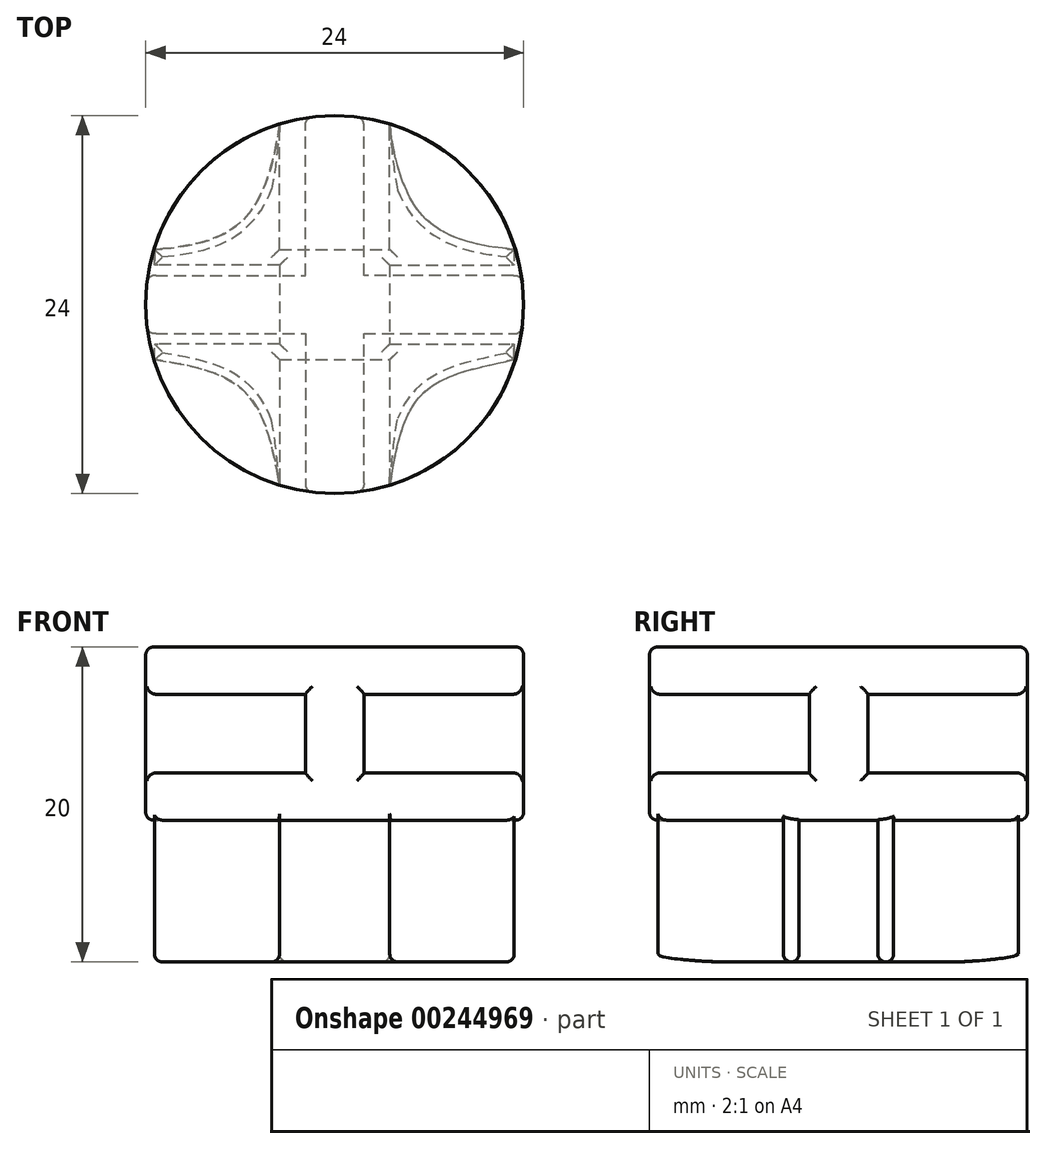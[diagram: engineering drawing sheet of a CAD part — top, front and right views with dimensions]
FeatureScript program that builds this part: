
annotation { "Feature Type Name" : "Feature", "Feature Type Description" : "" }
export const myFeature = defineFeature(function(context is Context, id is Id, definition is map)
    precondition{}
    {
        {
            var Q0;
            Q0=qCreatedBy(makeId("Top.planeOp"),FACE);
            var sketch = newSketch(context, id + "F0", { "sketchPlane" : qUnion([Q0])});
            skCircle(sketch, "E0", {"center": v(0, 0) * mm, "radius": 12 * mm});
            skSolve(sketch);
        }
        {
            var Q0;
            Q0=makeQuery(id+"F0.imprint","IMPRINT",FACE,{"disambiguationData":[TD([[makeQuery(id+"F0.imprint","IMPRINT",EDGE,{"derivedFrom":sQuery(id+"F0.wireOp",EDGE,"E0")}),1.0]])]});
            extrude(context, id + "F1", {"entities" : qUnion([Q0]), "depth" : 3 * mm});
        }
        {
            var Q0;
            Q0=qCreatedBy(makeId("Top.planeOp"),FACE);
            var sketch = newSketch(context, id + "F2", { "sketchPlane" : qUnion([Q0])});
            skCircle(sketch, "E1", {"center": v(0, 0) * mm, "radius": 12 * mm});
            skLineSegment(sketch, "E2", {"start": v(1.86, 11.86) * mm, "end": v(1.86, 1.86) * mm});
            skLineSegment(sketch, "E3", {"start": v(1.86, 1.86) * mm, "end": v(11.86, 1.86) * mm});
            skLineSegment(sketch, "E4", {"start": v(11.86, -1.86) * mm, "end": v(1.86, -1.86) * mm});
            skLineSegment(sketch, "E5", {"start": v(1.86, -1.86) * mm, "end": v(1.86, -11.86) * mm});
            skLineSegment(sketch, "E6", {"start": v(-1.86, 11.86) * mm, "end": v(-1.86, 1.86) * mm});
            skLineSegment(sketch, "E7", {"start": v(-1.86, 1.86) * mm, "end": v(-11.86, 1.86) * mm});
            skLineSegment(sketch, "E8", {"start": v(-1.86, -11.86) * mm, "end": v(-1.86, -1.86) * mm});
            skLineSegment(sketch, "E9", {"start": v(-1.86, -1.86) * mm, "end": v(-11.86, -1.86) * mm});
            skSolve(sketch);
        }
        {
            var Q0;
            {var subQ5=sQuery(id+"F2.wireOp",EDGE,"E2");Q0=makeQuery(id+"F2.imprint","IMPRINT",FACE,{"disambiguationData":[TD([[makeQuery(id+"F2.imprint","IMPRINT",EDGE,{"derivedFrom":subQ5}),-1.0]])]});}
            extrude(context, id + "F3", {"entities" : qUnion([Q0]), "operationType" : NewBodyOperationType.ADD, "depth" : 8 * mm});
        }
        {
            var Q0;
            Q0=makeQuery(id+"F3.opExtrude","CAP_FACE",FACE,{"disambiguationData":[OSD([sQuery(id+"F2.wireOp",EDGE,"E1"),sQuery(id+"F2.wireOp",EDGE,"E2"),sQuery(id+"F2.wireOp",EDGE,"E3"),sQuery(id+"F2.wireOp",EDGE,"E4"),sQuery(id+"F2.wireOp",EDGE,"E5"),sQuery(id+"F2.wireOp",EDGE,"E6"),sQuery(id+"F2.wireOp",EDGE,"E7"),sQuery(id+"F2.wireOp",EDGE,"E8"),sQuery(id+"F2.wireOp",EDGE,"E9")])],"isStart":false});
            var sketch = newSketch(context, id + "F4", { "sketchPlane" : qUnion([Q0])});
            skCircle(sketch, "E10", {"center": v(0, 0) * mm, "radius": 12 * mm});
            skSolve(sketch);
        }
        {
            var Q0;
            {var subQ1=makeQuery(id+"F3.opExtrude","CAP_EDGE",EDGE,{"disambiguationData":[OSD([sQuery(id+"F2.wireOp",EDGE,"E8")])],"isStart":false});Q0=makeQuery(id+"F4.imprint","IMPRINT",FACE,{"disambiguationData":[TD([[makeQuery(id+"F4.imprint","IMPRINT",EDGE,{"derivedFrom":subQ1}),1.0]])]});}
            var Q1;
            {var subQ6=makeQuery(id+"F3.opExtrude","CAP_EDGE",EDGE,{"disambiguationData":[OSD([sQuery(id+"F2.wireOp",EDGE,"E2")])],"isStart":false});Q1=makeQuery(id+"F4.imprint","IMPRINT",FACE,{"disambiguationData":[TD([[makeQuery(id+"F4.imprint","IMPRINT",EDGE,{"derivedFrom":subQ6}),-1.0]])]});}
            var Q2;
            {var subQ1=makeQuery(id+"F3.opExtrude","CAP_EDGE",EDGE,{"disambiguationData":[OSD([sQuery(id+"F2.wireOp",EDGE,"E4")])],"isStart":false});Q2=makeQuery(id+"F4.imprint","IMPRINT",FACE,{"disambiguationData":[TD([[makeQuery(id+"F4.imprint","IMPRINT",EDGE,{"derivedFrom":subQ1}),1.0]])]});}
            var Q3;
            {var subQ1=makeQuery(id+"F3.opExtrude","CAP_EDGE",EDGE,{"disambiguationData":[OSD([sQuery(id+"F2.wireOp",EDGE,"E2")])],"isStart":false});Q3=makeQuery(id+"F4.imprint","IMPRINT",FACE,{"disambiguationData":[TD([[makeQuery(id+"F4.imprint","IMPRINT",EDGE,{"derivedFrom":subQ1}),1.0]])]});}
            var Q4;
            {var subQ1=makeQuery(id+"F3.opExtrude","CAP_EDGE",EDGE,{"disambiguationData":[OSD([sQuery(id+"F2.wireOp",EDGE,"E6")])],"isStart":false});Q4=makeQuery(id+"F4.imprint","IMPRINT",FACE,{"disambiguationData":[TD([[makeQuery(id+"F4.imprint","IMPRINT",EDGE,{"derivedFrom":subQ1}),-1.0]])]});}
            extrude(context, id + "F5", {"entities" : qUnion([Q0, Q1, Q2, Q3, Q4]), "operationType" : NewBodyOperationType.ADD, "depth" : 3 * mm});
        }
        {
            var Q0;
            Q0=qCreatedBy(makeId("Top.planeOp"),FACE);
            var sketch = newSketch(context, id + "F6", { "sketchPlane" : qUnion([Q0])});
            skLineSegment(sketch, "E11.bottom", {"start": v(-3.5, 3.5) * mm, "end": v(3.5, 3.5) * mm});
            skLineSegment(sketch, "E11.top", {"start": v(-3.5, -3.5) * mm, "end": v(3.5, -3.5) * mm});
            skLineSegment(sketch, "E11.left", {"start": v(-3.5, 3.5) * mm, "end": v(-3.5, -3.5) * mm});
            skLineSegment(sketch, "E11.right", {"start": v(3.5, 3.5) * mm, "end": v(3.5, -3.5) * mm});
            skPoint(sketch, "E11.middle", {"position": v(0, 0) * mm});
            skLineSegment(sketch, "E12.bottom", {"start": v(3.5, -3.5) * mm, "end": v(2.5, -3.5) * mm});
            skLineSegment(sketch, "E12.top", {"start": v(3.5, -11.47) * mm, "end": v(2.5, -11.47) * mm});
            skLineSegment(sketch, "E12.left", {"start": v(3.5, -3.5) * mm, "end": v(3.5, -11.47) * mm});
            skLineSegment(sketch, "E12.right", {"start": v(2.5, -3.5) * mm, "end": v(2.5, -11.47) * mm});
            skLineSegment(sketch, "E13.bottom", {"start": v(-3.5, -3.5) * mm, "end": v(-2.5, -3.5) * mm});
            skLineSegment(sketch, "E13.top", {"start": v(-3.5, -11.47) * mm, "end": v(-2.5, -11.47) * mm});
            skLineSegment(sketch, "E13.left", {"start": v(-3.5, -3.5) * mm, "end": v(-3.5, -11.47) * mm});
            skLineSegment(sketch, "E13.right", {"start": v(-2.5, -3.5) * mm, "end": v(-2.5, -11.47) * mm});
            skLineSegment(sketch, "E14.bottom", {"start": v(3.5, -3.5) * mm, "end": v(11.4, -3.5) * mm});
            skLineSegment(sketch, "E14.top", {"start": v(3.5, -2.5) * mm, "end": v(11.4, -2.5) * mm});
            skLineSegment(sketch, "E14.left", {"start": v(3.5, -3.5) * mm, "end": v(3.5, -2.5) * mm});
            skLineSegment(sketch, "E14.right", {"start": v(11.4, -3.5) * mm, "end": v(11.4, -2.5) * mm});
            skLineSegment(sketch, "E15.bottom", {"start": v(3.5, 3.5) * mm, "end": v(11.4, 3.5) * mm});
            skLineSegment(sketch, "E15.top", {"start": v(3.5, 2.5) * mm, "end": v(11.4, 2.5) * mm});
            skLineSegment(sketch, "E15.left", {"start": v(3.5, 3.5) * mm, "end": v(3.5, 2.5) * mm});
            skLineSegment(sketch, "E15.right", {"start": v(11.4, 3.5) * mm, "end": v(11.4, 2.5) * mm});
            skLineSegment(sketch, "E16.bottom", {"start": v(-3.5, 3.5) * mm, "end": v(-11.45, 3.5) * mm});
            skLineSegment(sketch, "E16.top", {"start": v(-3.5, 2.5) * mm, "end": v(-11.45, 2.5) * mm});
            skLineSegment(sketch, "E16.left", {"start": v(-3.5, 3.5) * mm, "end": v(-3.5, 2.5) * mm});
            skLineSegment(sketch, "E16.right", {"start": v(-11.45, 3.5) * mm, "end": v(-11.45, 2.5) * mm});
            skLineSegment(sketch, "E17.bottom", {"start": v(-3.5, -3.5) * mm, "end": v(-11.45, -3.5) * mm});
            skLineSegment(sketch, "E17.top", {"start": v(-3.5, -2.5) * mm, "end": v(-11.45, -2.5) * mm});
            skLineSegment(sketch, "E17.left", {"start": v(-3.5, -3.5) * mm, "end": v(-3.5, -2.5) * mm});
            skLineSegment(sketch, "E17.right", {"start": v(-11.45, -3.5) * mm, "end": v(-11.45, -2.5) * mm});
            skLineSegment(sketch, "E18.bottom", {"start": v(3.5, 3.5) * mm, "end": v(2.5, 3.5) * mm});
            skLineSegment(sketch, "E18.top", {"start": v(3.5, 11.43) * mm, "end": v(2.5, 11.43) * mm});
            skLineSegment(sketch, "E18.left", {"start": v(3.5, 3.5) * mm, "end": v(3.5, 11.43) * mm});
            skLineSegment(sketch, "E18.right", {"start": v(2.5, 3.5) * mm, "end": v(2.5, 11.43) * mm});
            skLineSegment(sketch, "E19.bottom", {"start": v(-3.5, 3.5) * mm, "end": v(-2.5, 3.5) * mm});
            skLineSegment(sketch, "E19.top", {"start": v(-3.5, 11.38) * mm, "end": v(-2.5, 11.38) * mm});
            skLineSegment(sketch, "E19.left", {"start": v(-3.5, 3.5) * mm, "end": v(-3.5, 11.38) * mm});
            skLineSegment(sketch, "E19.right", {"start": v(-2.5, 3.5) * mm, "end": v(-2.5, 11.38) * mm});
            skFitSpline(sketch, "E20", {"points": [v(3.5, -11.47) * mm, v(5.52, -5.72) * mm, v(11.4, -3.5) * mm], "startDerivative": vector(2.5, 13.03) * mm, "endDerivative": vector(13.28, 2.93) * mm});
            skFitSpline(sketch, "E21", {"points": [v(-3.5, -11.47) * mm, v(-5.72, -5.52) * mm, v(-11.45, -3.5) * mm], "startDerivative": vector(-2.47, 13.8) * mm, "endDerivative": vector(-13.47, 2.1) * mm});
            skFitSpline(sketch, "E22", {"points": [v(-11.45, 3.5) * mm, v(-5.91, 5.28) * mm, v(-3.5, 11.38) * mm], "startDerivative": vector(13.8, 1.03) * mm, "endDerivative": vector(2.19, 14.62) * mm});
            skFitSpline(sketch, "E23", {"points": [v(11.4, 3.5) * mm, v(5.8, 5.42) * mm, v(3.5, 11.43) * mm], "startDerivative": vector(-14.02, 1.2) * mm, "endDerivative": vector(-1.85, 14.6) * mm});
            skSolve(sketch);
        }
        {
            var Q0;
            Q0=makeQuery(id+"F6.imprint","IMPRINT",FACE,{"disambiguationData":[TD([[makeQuery(id+"F6.imprint","IMPRINT",EDGE,{"derivedFrom":sQuery(id+"F6.wireOp",EDGE,"E12.bottom")}),1.0]])]});
            var Q1;
            Q1=makeQuery(id+"F6.imprint","IMPRINT",FACE,{"disambiguationData":[TD([[makeQuery(id+"F6.imprint","IMPRINT",EDGE,{"derivedFrom":sQuery(id+"F6.wireOp",EDGE,"E12.left")}),1.0]])]});
            var Q2;
            Q2=makeQuery(id+"F6.imprint","IMPRINT",FACE,{"disambiguationData":[TD([[makeQuery(id+"F6.imprint","IMPRINT",EDGE,{"derivedFrom":sQuery(id+"F6.wireOp",EDGE,"E14.bottom")}),1.0]])]});
            var Q3;
            Q3=makeQuery(id+"F6.imprint","IMPRINT",FACE,{"disambiguationData":[TD([[makeQuery(id+"F6.imprint","IMPRINT",EDGE,{"derivedFrom":sQuery(id+"F6.wireOp",EDGE,"E11.bottom")}),-1.0]])]});
            var Q4;
            Q4=makeQuery(id+"F6.imprint","IMPRINT",FACE,{"disambiguationData":[TD([[makeQuery(id+"F6.imprint","IMPRINT",EDGE,{"derivedFrom":sQuery(id+"F6.wireOp",EDGE,"E13.bottom")}),-1.0]])]});
            var Q5;
            Q5=makeQuery(id+"F6.imprint","IMPRINT",FACE,{"disambiguationData":[TD([[makeQuery(id+"F6.imprint","IMPRINT",EDGE,{"derivedFrom":sQuery(id+"F6.wireOp",EDGE,"E13.left")}),-1.0]])]});
            var Q6;
            Q6=makeQuery(id+"F6.imprint","IMPRINT",FACE,{"disambiguationData":[TD([[makeQuery(id+"F6.imprint","IMPRINT",EDGE,{"derivedFrom":sQuery(id+"F6.wireOp",EDGE,"E17.bottom")}),-1.0]])]});
            var Q7;
            Q7=makeQuery(id+"F6.imprint","IMPRINT",FACE,{"disambiguationData":[TD([[makeQuery(id+"F6.imprint","IMPRINT",EDGE,{"derivedFrom":sQuery(id+"F6.wireOp",EDGE,"E16.bottom")}),-1.0]])]});
            var Q8;
            Q8=makeQuery(id+"F6.imprint","IMPRINT",FACE,{"disambiguationData":[TD([[makeQuery(id+"F6.imprint","IMPRINT",EDGE,{"derivedFrom":sQuery(id+"F6.wireOp",EDGE,"E16.bottom")}),1.0]])]});
            var Q9;
            Q9=makeQuery(id+"F6.imprint","IMPRINT",FACE,{"disambiguationData":[TD([[makeQuery(id+"F6.imprint","IMPRINT",EDGE,{"derivedFrom":sQuery(id+"F6.wireOp",EDGE,"E19.bottom")}),1.0]])]});
            var Q10;
            Q10=makeQuery(id+"F6.imprint","IMPRINT",FACE,{"disambiguationData":[TD([[makeQuery(id+"F6.imprint","IMPRINT",EDGE,{"derivedFrom":sQuery(id+"F6.wireOp",EDGE,"E15.bottom")}),1.0]])]});
            var Q11;
            Q11=makeQuery(id+"F6.imprint","IMPRINT",FACE,{"disambiguationData":[TD([[makeQuery(id+"F6.imprint","IMPRINT",EDGE,{"derivedFrom":sQuery(id+"F6.wireOp",EDGE,"E15.bottom")}),-1.0]])]});
            var Q12;
            Q12=makeQuery(id+"F6.imprint","IMPRINT",FACE,{"disambiguationData":[TD([[makeQuery(id+"F6.imprint","IMPRINT",EDGE,{"derivedFrom":sQuery(id+"F6.wireOp",EDGE,"E18.bottom")}),-1.0]])]});
            extrude(context, id + "F7", {"entities" : qUnion([Q0, Q1, Q2, Q3, Q4, Q5, Q6, Q7, Q8, Q9, Q10, Q11, Q12]), "operationType" : NewBodyOperationType.ADD, "oppositeDirection" : true, "depth" : 9 * mm});
        }
        {
            var Q0;
            Q0=makeQuery(id+"F3.opExtrude","SWEPT_EDGE",EDGE,{"disambiguationData":[OSD([sQuery(id+"F2.wireOp",EDGE,"E1"),sQuery(id+"F2.wireOp",EDGE,"E2")])]});
            var Q1;
            {var subQ1=sQuery(id+"F4.wireOp",EDGE,"E10");var subQ2=sQuery(id+"F2.wireOp",EDGE,"E2");Q1=makeQuery(id+"F5.boolean.opBoolean","SPLIT",EDGE,{"disambiguationData":[TD([makeQuery(id+"F3.opExtrude","SWEPT_FACE",FACE,{"disambiguationData":[OSD([subQ2])]})])],"derivedFrom":makeQuery(id+"F5.opExtrude","CAP_EDGE",EDGE,{"disambiguationData":[OSD([subQ1])],"isStart":true})});}
            var Q2;
            Q2=makeQuery(id+"F3.opExtrude","SWEPT_EDGE",EDGE,{"disambiguationData":[OSD([sQuery(id+"F2.wireOp",EDGE,"E1"),sQuery(id+"F2.wireOp",EDGE,"E3")])]});
            var Q3;
            {var subQ0=sQuery(id+"F0.wireOp",EDGE,"E0");var subQ2=sQuery(id+"F2.wireOp",EDGE,"E2");Q3=makeQuery(id+"F3.boolean.opBoolean","SPLIT",EDGE,{"disambiguationData":[TD([makeQuery(id+"F3.opExtrude","SWEPT_FACE",FACE,{"disambiguationData":[OSD([subQ2])]})])],"derivedFrom":makeQuery(id+"F1.opExtrude","CAP_EDGE",EDGE,{"disambiguationData":[OSD([subQ0])],"isStart":false})});}
            var Q4;
            Q4=makeQuery(id+"F5.opExtrude","CAP_EDGE",EDGE,{"disambiguationData":[OSD([sQuery(id+"F4.wireOp",EDGE,"E10")])],"isStart":false});
            var Q5;
            Q5=makeQuery(id+"F3.opExtrude","SWEPT_EDGE",EDGE,{"disambiguationData":[OSD([sQuery(id+"F2.wireOp",EDGE,"E1"),sQuery(id+"F2.wireOp",EDGE,"E4")])]});
            var Q6;
            {var subQ0=sQuery(id+"F0.wireOp",EDGE,"E0");var subQ3=sQuery(id+"F2.wireOp",EDGE,"E4");Q6=makeQuery(id+"F3.boolean.opBoolean","SPLIT",EDGE,{"disambiguationData":[TD([makeQuery(id+"F3.opExtrude","SWEPT_FACE",FACE,{"disambiguationData":[OSD([subQ3])]})])],"derivedFrom":makeQuery(id+"F1.opExtrude","CAP_EDGE",EDGE,{"disambiguationData":[OSD([subQ0])],"isStart":false})});}
            var Q7;
            {var subQ2=sQuery(id+"F4.wireOp",EDGE,"E10");var subQ3=sQuery(id+"F2.wireOp",EDGE,"E4");Q7=makeQuery(id+"F5.boolean.opBoolean","SPLIT",EDGE,{"disambiguationData":[TD([makeQuery(id+"F3.opExtrude","SWEPT_FACE",FACE,{"disambiguationData":[OSD([subQ3])]})])],"derivedFrom":makeQuery(id+"F5.opExtrude","CAP_EDGE",EDGE,{"disambiguationData":[OSD([subQ2])],"isStart":true})});}
            var Q8;
            Q8=makeQuery(id+"F3.opExtrude","SWEPT_EDGE",EDGE,{"disambiguationData":[OSD([sQuery(id+"F2.wireOp",EDGE,"E1"),sQuery(id+"F2.wireOp",EDGE,"E5")])]});
            var Q9;
            Q9=makeQuery(id+"F3.opExtrude","SWEPT_EDGE",EDGE,{"disambiguationData":[OSD([sQuery(id+"F2.wireOp",EDGE,"E1"),sQuery(id+"F2.wireOp",EDGE,"E8")])]});
            var Q10;
            {var subQ0=sQuery(id+"F0.wireOp",EDGE,"E0");var subQ3=sQuery(id+"F2.wireOp",EDGE,"E8");Q10=makeQuery(id+"F3.boolean.opBoolean","SPLIT",EDGE,{"disambiguationData":[TD([makeQuery(id+"F3.opExtrude","SWEPT_FACE",FACE,{"disambiguationData":[OSD([subQ3])]})])],"derivedFrom":makeQuery(id+"F1.opExtrude","CAP_EDGE",EDGE,{"disambiguationData":[OSD([subQ0])],"isStart":false})});}
            var Q11;
            {var subQ1=sQuery(id+"F2.wireOp",EDGE,"E8");var subQ2=sQuery(id+"F4.wireOp",EDGE,"E10");Q11=makeQuery(id+"F5.boolean.opBoolean","SPLIT",EDGE,{"disambiguationData":[TD([makeQuery(id+"F3.opExtrude","SWEPT_FACE",FACE,{"disambiguationData":[OSD([subQ1])]})])],"derivedFrom":makeQuery(id+"F5.opExtrude","CAP_EDGE",EDGE,{"disambiguationData":[OSD([subQ2])],"isStart":true})});}
            var Q12;
            Q12=makeQuery(id+"F3.opExtrude","SWEPT_EDGE",EDGE,{"disambiguationData":[OSD([sQuery(id+"F2.wireOp",EDGE,"E1"),sQuery(id+"F2.wireOp",EDGE,"E9")])]});
            var Q13;
            Q13=makeQuery(id+"F3.opExtrude","SWEPT_EDGE",EDGE,{"disambiguationData":[OSD([sQuery(id+"F2.wireOp",EDGE,"E1"),sQuery(id+"F2.wireOp",EDGE,"E7")])]});
            var Q14;
            {var subQ0=sQuery(id+"F0.wireOp",EDGE,"E0");var subQ1=sQuery(id+"F2.wireOp",EDGE,"E6");Q14=makeQuery(id+"F3.boolean.opBoolean","SPLIT",EDGE,{"disambiguationData":[TD([makeQuery(id+"F3.opExtrude","SWEPT_FACE",FACE,{"disambiguationData":[OSD([subQ1])]})])],"derivedFrom":makeQuery(id+"F1.opExtrude","CAP_EDGE",EDGE,{"disambiguationData":[OSD([subQ0])],"isStart":false})});}
            var Q15;
            {var subQ1=sQuery(id+"F4.wireOp",EDGE,"E10");var subQ3=sQuery(id+"F2.wireOp",EDGE,"E6");Q15=makeQuery(id+"F5.boolean.opBoolean","SPLIT",EDGE,{"disambiguationData":[TD([makeQuery(id+"F3.opExtrude","SWEPT_FACE",FACE,{"disambiguationData":[OSD([subQ3])]})])],"derivedFrom":makeQuery(id+"F5.opExtrude","CAP_EDGE",EDGE,{"disambiguationData":[OSD([subQ1])],"isStart":true})});}
            var Q16;
            Q16=makeQuery(id+"F3.opExtrude","SWEPT_EDGE",EDGE,{"disambiguationData":[OSD([sQuery(id+"F2.wireOp",EDGE,"E1"),sQuery(id+"F2.wireOp",EDGE,"E6")])]});
            var Q17;
            Q17=makeQuery(id+"F7.opExtrude","CAP_FACE",FACE,{"disambiguationData":[OSD([sQuery(id+"F6.wireOp",EDGE,"E11.bottom"),sQuery(id+"F6.wireOp",EDGE,"E11.top"),sQuery(id+"F6.wireOp",EDGE,"E11.left"),sQuery(id+"F6.wireOp",EDGE,"E11.right"),sQuery(id+"F6.wireOp",EDGE,"E12.top"),sQuery(id+"F6.wireOp",EDGE,"E12.right"),sQuery(id+"F6.wireOp",EDGE,"E13.top"),sQuery(id+"F6.wireOp",EDGE,"E13.right"),sQuery(id+"F6.wireOp",EDGE,"E14.top"),sQuery(id+"F6.wireOp",EDGE,"E14.right"),sQuery(id+"F6.wireOp",EDGE,"E15.top"),sQuery(id+"F6.wireOp",EDGE,"E15.right"),sQuery(id+"F6.wireOp",EDGE,"E16.top"),sQuery(id+"F6.wireOp",EDGE,"E16.right"),sQuery(id+"F6.wireOp",EDGE,"E17.top"),sQuery(id+"F6.wireOp",EDGE,"E17.right"),sQuery(id+"F6.wireOp",EDGE,"E18.top"),sQuery(id+"F6.wireOp",EDGE,"E18.right"),sQuery(id+"F6.wireOp",EDGE,"E19.top"),sQuery(id+"F6.wireOp",EDGE,"E19.right"),sQuery(id+"F6.wireOp",EDGE,"E20"),sQuery(id+"F6.wireOp",EDGE,"E21"),sQuery(id+"F6.wireOp",EDGE,"E22"),sQuery(id+"F6.wireOp",EDGE,"E23")])],"isStart":false});
            var Q18;
            Q18=makeQuery(id+"F1.opExtrude","CAP_EDGE",EDGE,{"disambiguationData":[OSD([sQuery(id+"F0.wireOp",EDGE,"E0")])],"isStart":true});
            fillet(context, id + "F8", {"entities" : qUnion([Q0, Q1, Q2, Q3, Q4, Q5, Q6, Q7, Q8, Q9, Q10, Q11, Q12, Q13, Q14, Q15, Q16, Q17, Q18]), "radius" : .5 * mm, "tangentPropagation" : true, "allowEdgeOverflow" : false});
        }
    });
